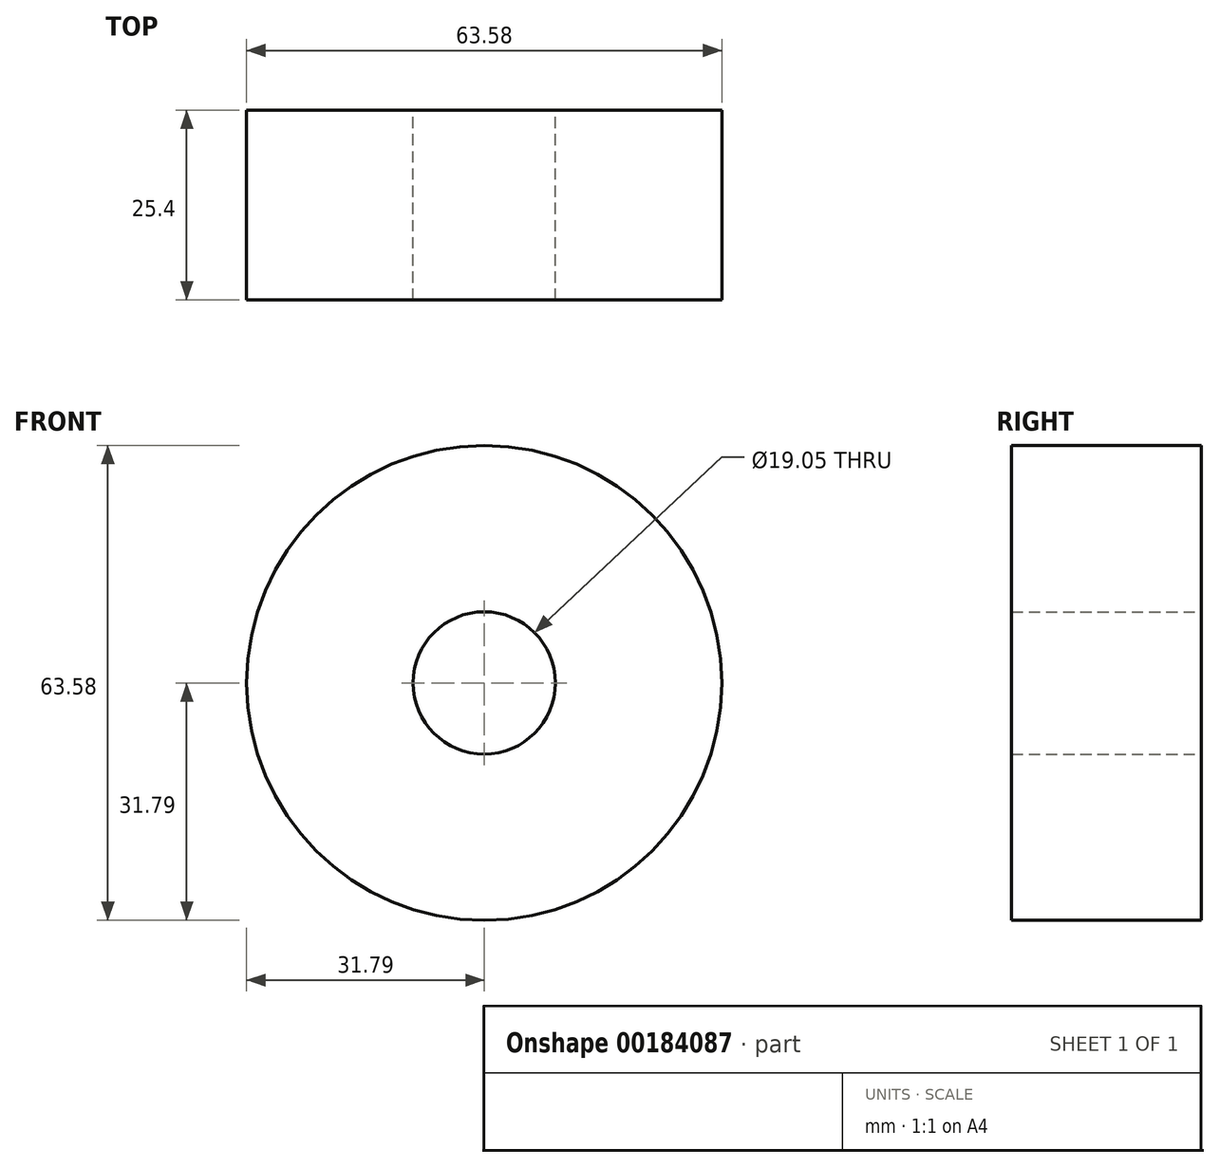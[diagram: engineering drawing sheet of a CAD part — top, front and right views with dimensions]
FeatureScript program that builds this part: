
annotation { "Feature Type Name" : "Feature", "Feature Type Description" : "" }
export const myFeature = defineFeature(function(context is Context, id is Id, definition is map)
    precondition{}
    {
        {
            var Q0;
            Q0=qCreatedBy(makeId("Front.planeOp"),FACE);
            var sketch = newSketch(context, id + "F0", { "sketchPlane" : qUnion([Q0])});
            skCircle(sketch, "E0", {"center": v(0, 0) * mm, "radius": 31.79 * mm});
            skCircle(sketch, "E1", {"center": v(0, 0) * mm, "radius": 9.53 * mm});
            skSolve(sketch);
        }
        {
            var Q0;
            Q0=makeQuery(id+"F0.imprint","IMPRINT",FACE,{"disambiguationData":[TD([[makeQuery(id+"F0.imprint","IMPRINT",EDGE,{"derivedFrom":sQuery(id+"F0.wireOp",EDGE,"E0")}),1.0]])]});
            extrude(context, id + "F1", {"entities" : qUnion([Q0]), "depth" : 25.4 * mm});
        }
    });
